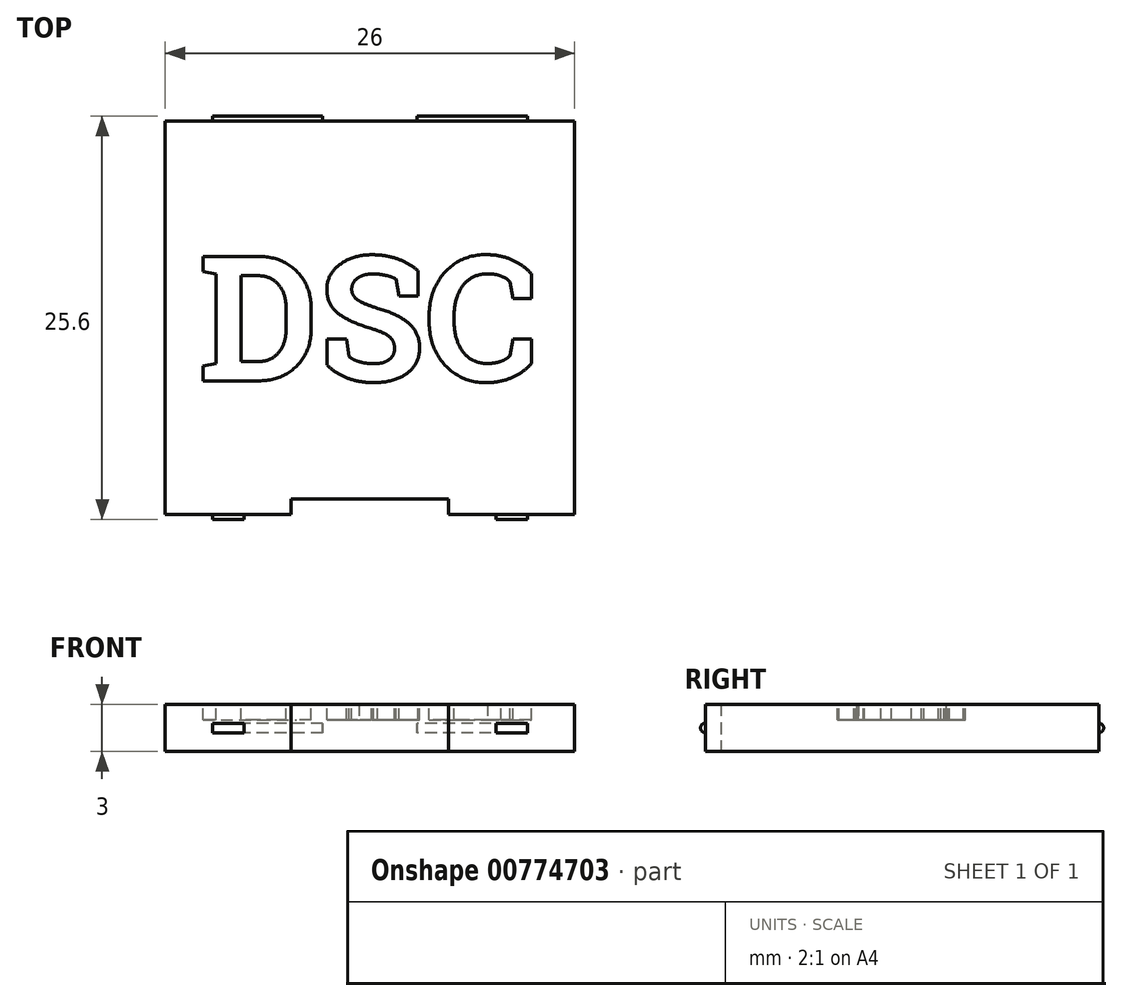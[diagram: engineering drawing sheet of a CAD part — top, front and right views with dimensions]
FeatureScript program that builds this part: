
annotation { "Feature Type Name" : "Feature", "Feature Type Description" : "" }
export const myFeature = defineFeature(function(context is Context, id is Id, definition is map)
    precondition{}
    {
        {
            var Q0;
            Q0=qCreatedBy(makeId("Top.planeOp"),FACE);
            var sketch = newSketch(context, id + "F0", { "sketchPlane" : qUnion([Q0])});
            skLineSegment(sketch, "E0.bottom", {"start": v(-13, 12.5) * mm, "end": v(13, 12.5) * mm});
            skLineSegment(sketch, "E0.top", {"start": v(-13, -12.5) * mm, "end": v(-5, -12.5) * mm});
            skLineSegment(sketch, "E0.left", {"start": v(-13, 12.5) * mm, "end": v(-13, -12.5) * mm});
            skLineSegment(sketch, "E0.right", {"start": v(13, 12.5) * mm, "end": v(13, -12.5) * mm});
            skLineSegment(sketch, "E1.top", {"start": v(-5, -11.5) * mm, "end": v(5, -11.5) * mm});
            skLineSegment(sketch, "E1.left", {"start": v(-5, -12.5) * mm, "end": v(-5, -11.5) * mm});
            skLineSegment(sketch, "E1.right", {"start": v(5, -12.5) * mm, "end": v(5, -11.5) * mm});
            skLineSegment(sketch, "E2.trimOffspring", {"start": v(5, -12.5) * mm, "end": v(13, -12.5) * mm});
            skSolve(sketch);
        }
        {
            var Q0;
            Q0=makeQuery(id+"F0.imprint","IMPRINT",FACE,{"disambiguationData":[TD([[makeQuery(id+"F0.imprint","IMPRINT",EDGE,{"derivedFrom":sQuery(id+"F0.wireOp",EDGE,"E0.bottom")}),-1.0]])]});
            extrude(context, id + "F1", {"entities" : qUnion([Q0]), "depth" : 3 * mm, "offsetDistance" : 25 * mm});
        }
        {
            var Q0;
            Q0=makeQuery(id+"F1.opExtrude","CAP_FACE",FACE,{"disambiguationData":[OSD([sQuery(id+"F0.wireOp",EDGE,"E0.bottom"),sQuery(id+"F0.wireOp",EDGE,"E0.top"),sQuery(id+"F0.wireOp",EDGE,"E0.left"),sQuery(id+"F0.wireOp",EDGE,"E0.right"),sQuery(id+"F0.wireOp",EDGE,"E1.top"),sQuery(id+"F0.wireOp",EDGE,"E1.left"),sQuery(id+"F0.wireOp",EDGE,"E1.right"),sQuery(id+"F0.wireOp",EDGE,"E2.trimOffspring")])],"isStart":false});
            var sketch = newSketch(context, id + "F2", { "sketchPlane" : qUnion([Q0])});
            skText(sketch, "E3", { "text": "DSC", "fontName": "RobotoSlab-Bold.ttf"});
            const initialGuessF2  = {"E3": [-0.01092, -0.004, 1, 0, 0.008]};
            skSetInitialGuess(sketch, initialGuessF2);
            skSolve(sketch);
        }
        {
            var Q0;
            Q0=qSketchRegion(id+"F2",true);
            extrude(context, id + "F3", {"entities" : qUnion([Q0]), "operationType" : NewBodyOperationType.REMOVE, "oppositeDirection" : true, "depth" : 1 * mm, "offsetDistance" : 25 * mm});
        }
        {
            var Q0;
            Q0=makeQuery(id+"F1.opExtrude","SWEPT_FACE",FACE,{"disambiguationData":[OSD([sQuery(id+"F0.wireOp",EDGE,"E0.left")])]});
            var sketch = newSketch(context, id + "F4", { "sketchPlane" : qUnion([Q0])});
            skArc(sketch, "E4", {"start": v(-12.5, 1.8) * mm, "mid": v(-12.8, 1.5) * mm, "end": v(-12.5, 1.2) * mm});
            skArc(sketch, "E5", {"start": v(12.5, 1.2) * mm, "mid": v(12.8, 1.5) * mm, "end": v(12.5, 1.8) * mm});
            skSolve(sketch);
        }
        {
            var Q0;
            Q0=makeQuery(id+"F1.opExtrude","SWEPT_FACE",FACE,{"disambiguationData":[OSD([sQuery(id+"F0.wireOp",EDGE,"E0.left")])]});
            cPlane(context, id + "F5", {"entities" : qUnion([Q0]), "cplaneType" : CPlaneType.OFFSET, "offset" : 5 * mm, "oppositeDirection" : true, "width" : 150 * mm, "height" : 150 * mm});
        }
        {
            var Q0;
            Q0=qCreatedBy(id+"F5.planeOp",FACE);
            cPlane(context, id + "F6", {"entities" : qUnion([Q0]), "cplaneType" : CPlaneType.OFFSET, "offset" : 5 * mm, "oppositeDirection" : true, "width" : 150 * mm, "height" : 150 * mm});
        }
        {
            var Q0;
            Q0=qCreatedBy(id+"F6.planeOp",FACE);
            cPlane(context, id + "F7", {"entities" : qUnion([Q0]), "cplaneType" : CPlaneType.OFFSET, "offset" : 6 * mm, "oppositeDirection" : true, "width" : 150 * mm, "height" : 150 * mm});
        }
        {
            var Q0;
            Q0=qCreatedBy(id+"F7.planeOp",FACE);
            cPlane(context, id + "F8", {"entities" : qUnion([Q0]), "cplaneType" : CPlaneType.OFFSET, "offset" : 5 * mm, "oppositeDirection" : true, "width" : 150 * mm, "height" : 150 * mm});
        }
        {
            var Q0;
            Q0=qCreatedBy(id+"F5.planeOp",FACE);
            cPlane(context, id + "F9", {"entities" : qUnion([Q0]), "cplaneType" : CPlaneType.OFFSET, "offset" : 2 * mm, "width" : 150 * mm, "height" : 150 * mm});
        }
        {
            var Q0;
            Q0=qCreatedBy(id+"F8.planeOp",FACE);
            cPlane(context, id + "F10", {"entities" : qUnion([Q0]), "cplaneType" : CPlaneType.OFFSET, "offset" : 2 * mm, "oppositeDirection" : true, "width" : 150 * mm, "height" : 150 * mm});
        }
        {
            var Q0;
            {var subQ0=sQuery(id+"F4.wireOp",EDGE,"E4");Q0=makeQuery(id+"F4.imprint","IMPRINT",FACE,{"disambiguationData":[TD([[makeQuery(id+"F4.imprint","IMPRINT",EDGE,{"derivedFrom":subQ0}),1.0]])]});}
            var Q1;
            Q1=sQuery(id+"F4.wireOp",EDGE,"E4");
            var Q2;
            Q2=qCreatedBy(id+"F6.planeOp",FACE);
            var Q3;
            Q3=qCreatedBy(id+"F9.planeOp",FACE);
            extrude(context, id + "F11", {"entities" : qUnion([Q0]), "operationType" : NewBodyOperationType.ADD, "surfaceOperationType" : NewSurfaceOperationType.ADD, "surfaceEntities" : qUnion([Q1]), "endBound" : BoundingType.UP_TO_SURFACE, "oppositeDirection" : true, "depth" : 25 * mm, "endBoundEntityFace" : qUnion([Q2]), "offsetDistance" : 5 * mm, "offsetOppositeDirection" : true, "hasSecondDirection" : true, "secondDirectionBound" : SecondDirectionBoundingType.UP_TO_SURFACE, "secondDirectionOppositeDirection" : true, "secondDirectionDepth" : 25 * mm, "secondDirectionBoundEntityFace" : qUnion([Q3])});
        }
        {
            var Q0;
            {var subQ0=sQuery(id+"F4.wireOp",EDGE,"E4");Q0=makeQuery(id+"F4.imprint","IMPRINT",FACE,{"disambiguationData":[TD([[makeQuery(id+"F4.imprint","IMPRINT",EDGE,{"derivedFrom":subQ0}),1.0]])]});}
            var Q1;
            Q1=qCreatedBy(id+"F10.planeOp",FACE);
            var Q2;
            Q2=qCreatedBy(id+"F7.planeOp",FACE);
            extrude(context, id + "F12", {"entities" : qUnion([Q0]), "operationType" : NewBodyOperationType.ADD, "endBound" : BoundingType.UP_TO_SURFACE, "oppositeDirection" : true, "depth" : 25 * mm, "endBoundEntityFace" : qUnion([Q1]), "offsetDistance" : 25 * mm, "hasSecondDirection" : true, "secondDirectionBound" : SecondDirectionBoundingType.UP_TO_SURFACE, "secondDirectionOppositeDirection" : true, "secondDirectionDepth" : 25 * mm, "secondDirectionBoundEntityFace" : qUnion([Q2])});
        }
        {
            var Q0;
            {var subQ0=sQuery(id+"F4.wireOp",EDGE,"E5");Q0=makeQuery(id+"F4.imprint","IMPRINT",FACE,{"disambiguationData":[TD([[makeQuery(id+"F4.imprint","IMPRINT",EDGE,{"derivedFrom":subQ0}),1.0]])]});}
            var Q1;
            Q1=qCreatedBy(id+"F5.planeOp",FACE);
            var Q2;
            Q2=qCreatedBy(id+"F9.planeOp",FACE);
            extrude(context, id + "F13", {"entities" : qUnion([Q0]), "operationType" : NewBodyOperationType.ADD, "endBound" : BoundingType.UP_TO_SURFACE, "oppositeDirection" : true, "depth" : 25 * mm, "endBoundEntityFace" : qUnion([Q1]), "offsetDistance" : 25 * mm, "hasSecondDirection" : true, "secondDirectionBound" : SecondDirectionBoundingType.UP_TO_SURFACE, "secondDirectionOppositeDirection" : true, "secondDirectionDepth" : 25 * mm, "secondDirectionBoundEntityFace" : qUnion([Q2])});
        }
        {
            var Q0;
            {var subQ0=sQuery(id+"F4.wireOp",EDGE,"E5");Q0=makeQuery(id+"F4.imprint","IMPRINT",FACE,{"disambiguationData":[TD([[makeQuery(id+"F4.imprint","IMPRINT",EDGE,{"derivedFrom":subQ0}),1.0]])]});}
            var Q1;
            Q1=qCreatedBy(id+"F10.planeOp",FACE);
            var Q2;
            Q2=qCreatedBy(id+"F8.planeOp",FACE);
            extrude(context, id + "F14", {"entities" : qUnion([Q0]), "operationType" : NewBodyOperationType.ADD, "endBound" : BoundingType.UP_TO_SURFACE, "oppositeDirection" : true, "depth" : 25 * mm, "endBoundEntityFace" : qUnion([Q1]), "offsetDistance" : 25 * mm, "hasSecondDirection" : true, "secondDirectionBound" : SecondDirectionBoundingType.UP_TO_SURFACE, "secondDirectionOppositeDirection" : true, "secondDirectionDepth" : 25 * mm, "secondDirectionBoundEntityFace" : qUnion([Q2])});
        }
    });
